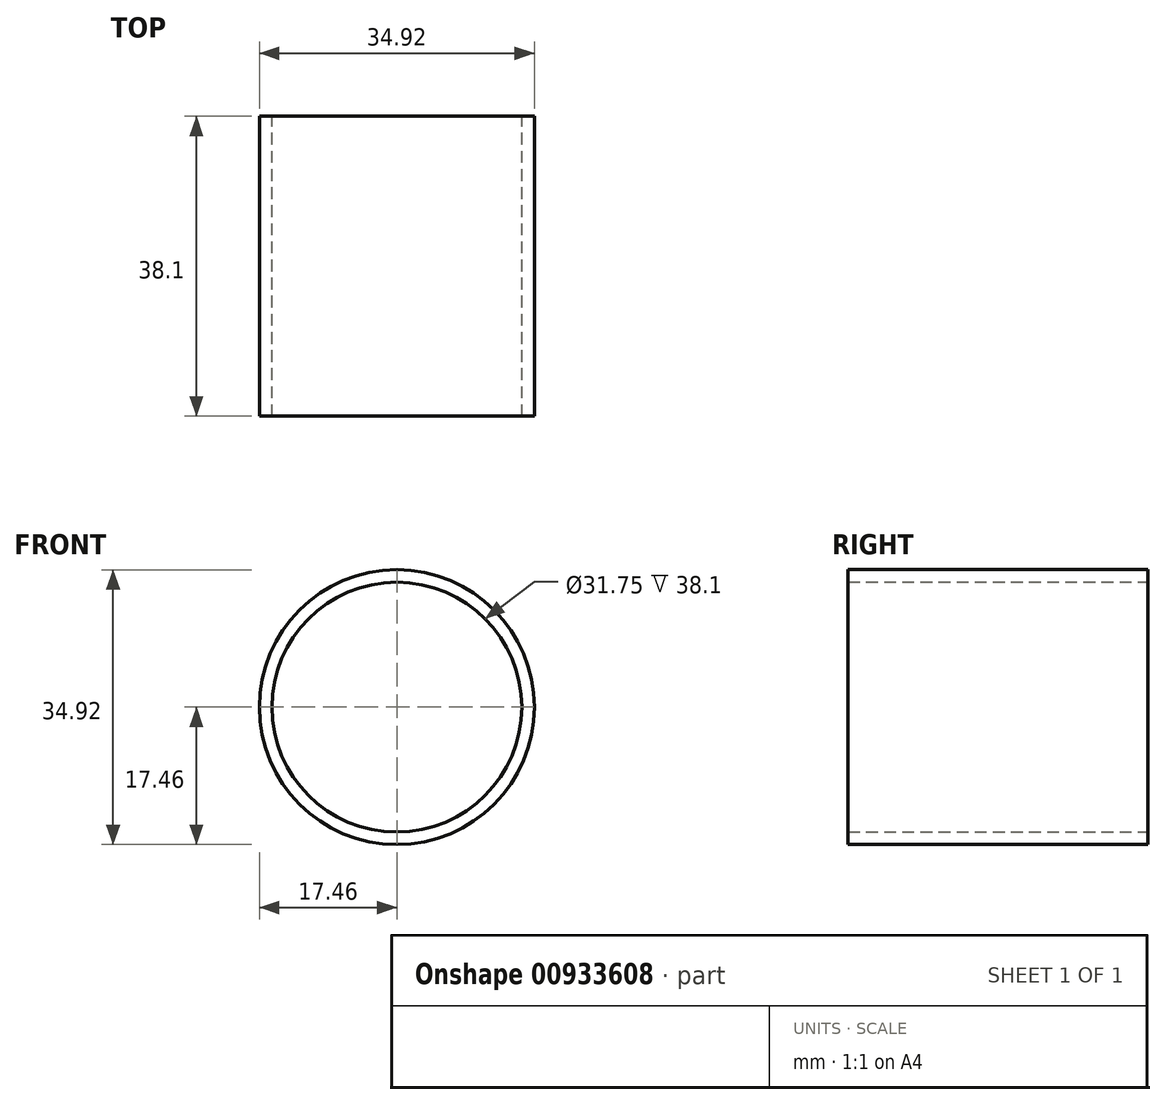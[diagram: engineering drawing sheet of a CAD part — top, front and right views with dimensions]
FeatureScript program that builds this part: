
annotation { "Feature Type Name" : "Feature", "Feature Type Description" : "" }
export const myFeature = defineFeature(function(context is Context, id is Id, definition is map)
    precondition{}
    {
        {
            var Q0;
            Q0=qCreatedBy(makeId("Front.planeOp"),FACE);
            var sketch = newSketch(context, id + "F0", { "sketchPlane" : qUnion([Q0])});
            skCircle(sketch, "E0", {"center": v(0, 0) * mm, "radius": 15.88 * mm});
            skCircle(sketch, "E1", {"center": v(0, 0) * mm, "radius": 17.46 * mm});
            skSolve(sketch);
        }
        {
            var Q0;
            Q0=makeQuery(id+"F0.imprint","IMPRINT",FACE,{"disambiguationData":[TD([[makeQuery(id+"F0.imprint","IMPRINT",EDGE,{"derivedFrom":sQuery(id+"F0.wireOp",EDGE,"E0")}),-1.0]])]});
            extrude(context, id + "F1", {"entities" : qUnion([Q0]), "depth" : 38.1 * mm, "offsetDistance" : 25.4 * mm});
        }
    });
